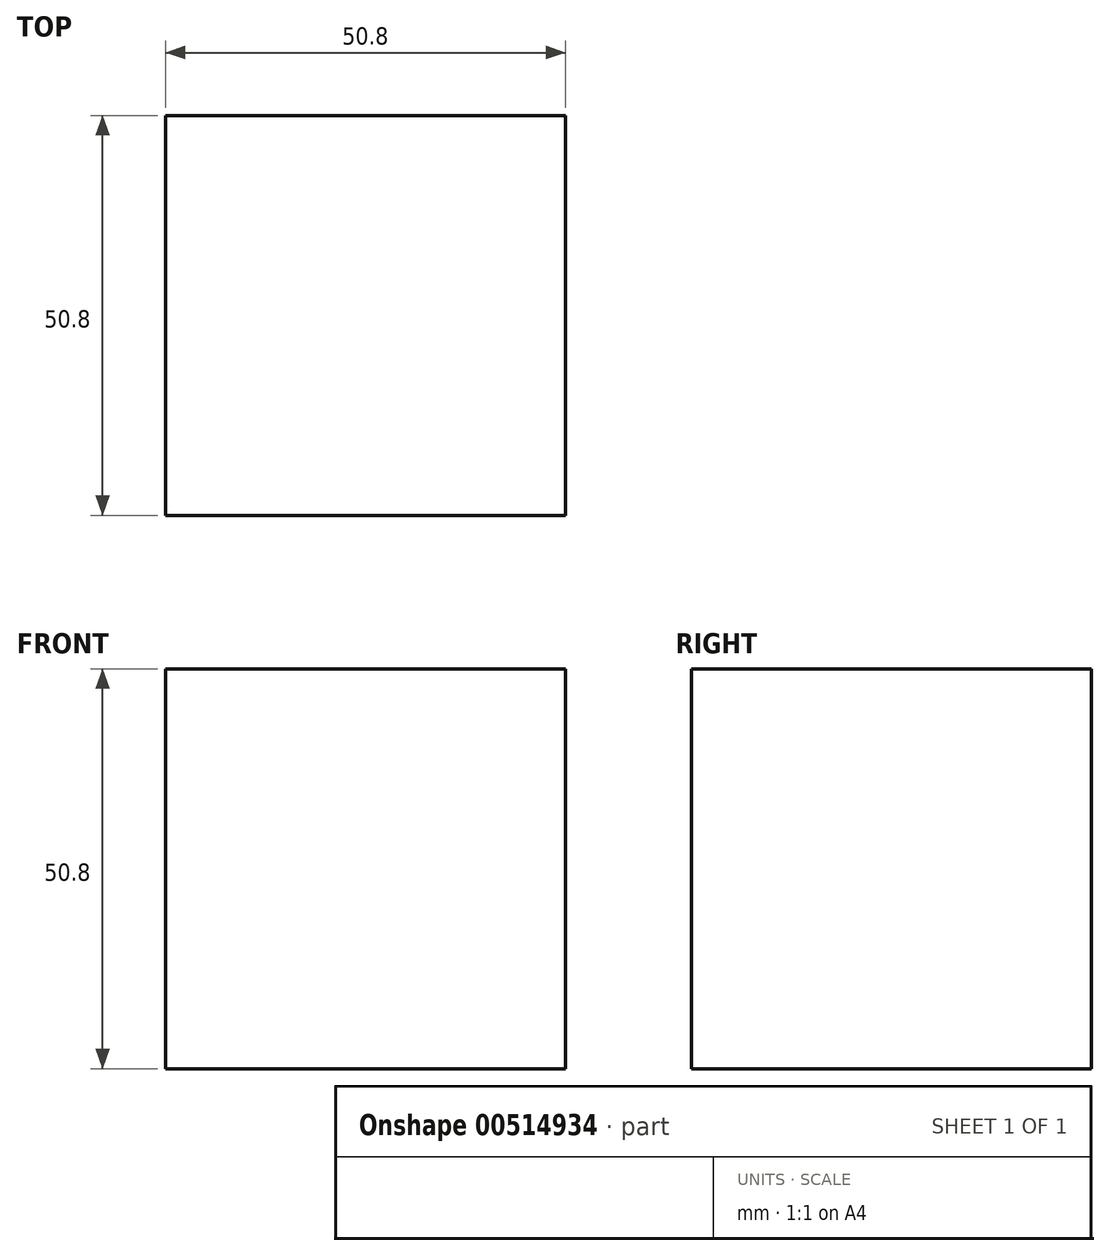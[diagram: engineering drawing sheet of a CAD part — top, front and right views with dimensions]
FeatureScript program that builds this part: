
annotation { "Feature Type Name" : "Feature", "Feature Type Description" : "" }
export const myFeature = defineFeature(function(context is Context, id is Id, definition is map)
    precondition{}
    {
        {
            var Q0;
            Q0=qCreatedBy(makeId("Front.planeOp"),FACE);
            var sketch = newSketch(context, id + "F0", { "sketchPlane" : qUnion([Q0])});
            skLineSegment(sketch, "E0.bottom", {"start": v(0, 0) * mm, "end": v(-50.8, 0) * mm});
            skLineSegment(sketch, "E0.top", {"start": v(0, 50.8) * mm, "end": v(-50.8, 50.8) * mm});
            skLineSegment(sketch, "E0.left", {"start": v(0, 0) * mm, "end": v(0, 50.8) * mm});
            skLineSegment(sketch, "E0.right", {"start": v(-50.8, 0) * mm, "end": v(-50.8, 50.8) * mm});
            skSolve(sketch);
        }
        {
            var Q0;
            Q0 = qSketchRegion(id + "F0", true);
            extrude(context, id + "F1", {"entities" : qUnion([Q0]), "depth" : 50.8 * mm, "offsetDistance" : 25.4 * mm});
        }
        {
            var Q0;
            Q0=qCreatedBy(makeId("Front.planeOp"),FACE);
            var sketch = newSketch(context, id + "F2", { "sketchPlane" : qUnion([Q0])});
            skLineSegment(sketch, "E1.bottom", {"start": v(0, 0) * mm, "end": v(-25.4, 0) * mm});
            skLineSegment(sketch, "E1.top", {"start": v(0, 25.4) * mm, "end": v(-25.4, 25.4) * mm});
            skLineSegment(sketch, "E1.left", {"start": v(0, 0) * mm, "end": v(0, 25.4) * mm});
            skLineSegment(sketch, "E1.right", {"start": v(-25.4, 0) * mm, "end": v(-25.4, 25.4) * mm});
            skSolve(sketch);
        }
        {
            var Q0;
            Q0 = qSketchRegion(id + "F2", true);
            extrude(context, id + "F3", {"entities" : qUnion([Q0]), "operationType" : NewBodyOperationType.REMOVE, "oppositeDirection" : true, "depth" : 25.4 * mm, "offsetDistance" : 25.4 * mm});
        }
        {
            var Q0;
            Q0=qCreatedBy(makeId("Front.planeOp"),FACE);
            var sketch = newSketch(context, id + "F4", { "sketchPlane" : qUnion([Q0])});
            skLineSegment(sketch, "E2.bottom", {"start": v(0, 0) * mm, "end": v(-25.4, 0) * mm});
            skLineSegment(sketch, "E2.top", {"start": v(0, 25.4) * mm, "end": v(-25.4, 25.4) * mm});
            skLineSegment(sketch, "E2.left", {"start": v(0, 0) * mm, "end": v(0, 25.4) * mm});
            skLineSegment(sketch, "E2.right", {"start": v(-25.4, 0) * mm, "end": v(-25.4, 25.4) * mm});
            skSolve(sketch);
        }
        {
            var Q0;
            Q0 = qSketchRegion(id + "F4", true);
            extrude(context, id + "F5", {"entities" : qUnion([Q0]), "operationType" : NewBodyOperationType.ADD, "depth" : 25.4 * mm, "offsetDistance" : 25.4 * mm});
        }
    });
